# Revit family: sh-al568
name_source: partatom
category: Lighting Fixtures
revit_build: Autodesk Revit 2017 (Build: 20160225_1515(x64)
units: mm (PartAtom-declared; Revit-internal decimal feet)

## family parameters
Always vertical = Yes
Cut with Voids When Loaded = No
Host = Ceiling
Light Source = Yes
OmniClass Number = 23.80.70.11
OmniClass Title = Luminaries for Internal Lighting
Part Type = Normal
Room Calculation Point = No
Round Connector Dimension = Use Diameter
Shared = No

## types (2) — shared parameters
Body Material = Aluminium
Body color = white body
Color Filter = 16777215
Default Elevation = 0.0 cm
Dimming Lamp Color Temperature Shift = <None>
Emit Shape Visible in Rendering = No
Emit from Circle Diameter = 5.0 cm
Flicker = Free Flicker
IP = IP20
Lamp = LED
Manufacturer = SHOA
Model = SH-AL568
Photometric Web File = CFAL568-12W.ies
Protection Class = class I
Tilt Angle = 90.00°
Type medule = COB
URL = https://www.shoaco.com
Voltage/Frequency = 230V-50HZ
Website = www.shoaco.com
color rendering index(CRI) = 80
consumption current = 0 A
instalation = Recessed
wattage. = 12 W

## per-type parameters (varying)
| type | Cutting Diameter | Diameter | Height | color temperature |
| SH-AL568(white Body-3000K-LED) | 80.0 cm | 90.0 cm | 72.5 cm | 3000 |
| SH-AL568(white Body-4000K-LED) | 8.0 cm | 9.0 cm | 6.8 cm | 4000 |

## geometry (parser evidence)
native form markers: Sweep x3
no freeform markers — native parametric forms only
